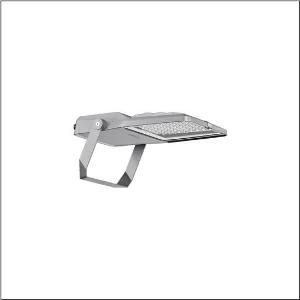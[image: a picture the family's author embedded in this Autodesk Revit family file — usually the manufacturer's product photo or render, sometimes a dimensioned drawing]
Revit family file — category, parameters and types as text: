
# Revit family: floodlight_fl_21_mini___pl52_5xa7775c2d1a_7e4d
name_source: partatom
category: Lighting Fixtures
units: mm (PartAtom-declared; Revit-internal decimal feet)

## family parameters
Cut with Voids When Loaded = No
Host = Face
Light Source = No
Part Type = Normal
Room Calculation Point = No
Round Connector Dimension = Use Diameter
Shared = No

## types (1)
- --- (1 x LED, 12190 lm, 89 W, 3000K)
    Apparent Load = 89 VA
    CIE Flux Codes = 26 60 98 100 100
    Color Rendering = 70
    Color Temperature = 3000K
    Default Elevation = 1800 mm
    Description = Floodlight FL 21 mini, floodlight, primary light control with lens, of PMMA, primary optical cover: protective disc, of toughened safety glass, transparent, light distribution: PL52, light emission: direct distribution, installation type: surface-mounted, LED, High Power LED, rated luminous flux: 12.190lm, luminous efficacy: 137lm/W, light colour: 730, colour temperature: 3000K, control gear: Smart Interface (Zhaga), control: flexible luminous flux parameterisation, time-dependent luminous flux control, constant luminous flux control, overheat protection, pre-setting: logarithmic dimming characteristic, with terminal, 6-pole, mains connection: 220..240V, AC, 50/60Hz, start of lifetime: 89W, end of service life: 94W, reduction: 43W, luminaire housing, of diecast aluminium, powder-coated, SITECO metallic grey (DB 702S), corrosivity category C5 mid according to DIN EN ISO 12944, suitable for swimming pools, chlorine-resistant, sealing non-destructively replaceable, mounting bracket, of steel, galvanised, powder-coated, SITECO metallic grey (DB 702S), Smart Interface above, protection rating (complete): IP66, insulation class (complete): insulation class II (safety insulation), certification: CE, ENEC, VDE, protection symbol: D, impact resistance: IK08, permissible operating ambient temperature: -40..+40°C, permissible operating ambient temperature for outdoor applications: -40..+50°C, standard: DIN EN 12944, LABS conformity tested according to VDMA 24364:2018-05, packaging unit: 1 piece

Light Distribution: PL52
    Height = 70 mm
    Lamp = 1 x LED
    Lamp Light Flux = 12190 lm
    Lamp Power = 89 W
    Lamp count = 1
    Length = 485 mm
    Luminous efficacy = 137 lm/W
    Manufacturer = Siteco
    ModVariant = No
    Model = 5XA7775C2D1A
    Mounting Place = Pole
    Mounting Type = Pole annexe
    Number of Poles = 1
    OnlyDefault = Yes
    Power Factor = 1
    Product Name = Floodlight FL 21 mini | PL52
    Product group = floodlight | pylon annexe
    ProductGroupID = 6201
    Protection Class = Protection class II
    Protection Degree = IP 66
    RLX_Detail_Level = 1
    RLX_Emergency_Light_Flux = 0 lm
    RLX_Emergency_Type = 0
    RLX_Emergency_Type_DB = No
    RlxData = <blob elided: 96105 chars, md5=3db0db61>
    Socket = socket
    Standby Power = 0 W
    System Light Flux = 12190 lm
    System Power = 89 W
    Type Comments = factory setting: luminous flux: 100 % | dim-lin: 254 | 456 mA
    Type Image = l_1006845.jpg
    URL = http://relux.com
    VarID = @adj_164377
    Voltage = 0 V
    Weight = 0.00 kg
    Width = 337 mm

## geometry (parser evidence)
native form markers: Blend x4, Sweep x13
no freeform markers — native parametric forms only
